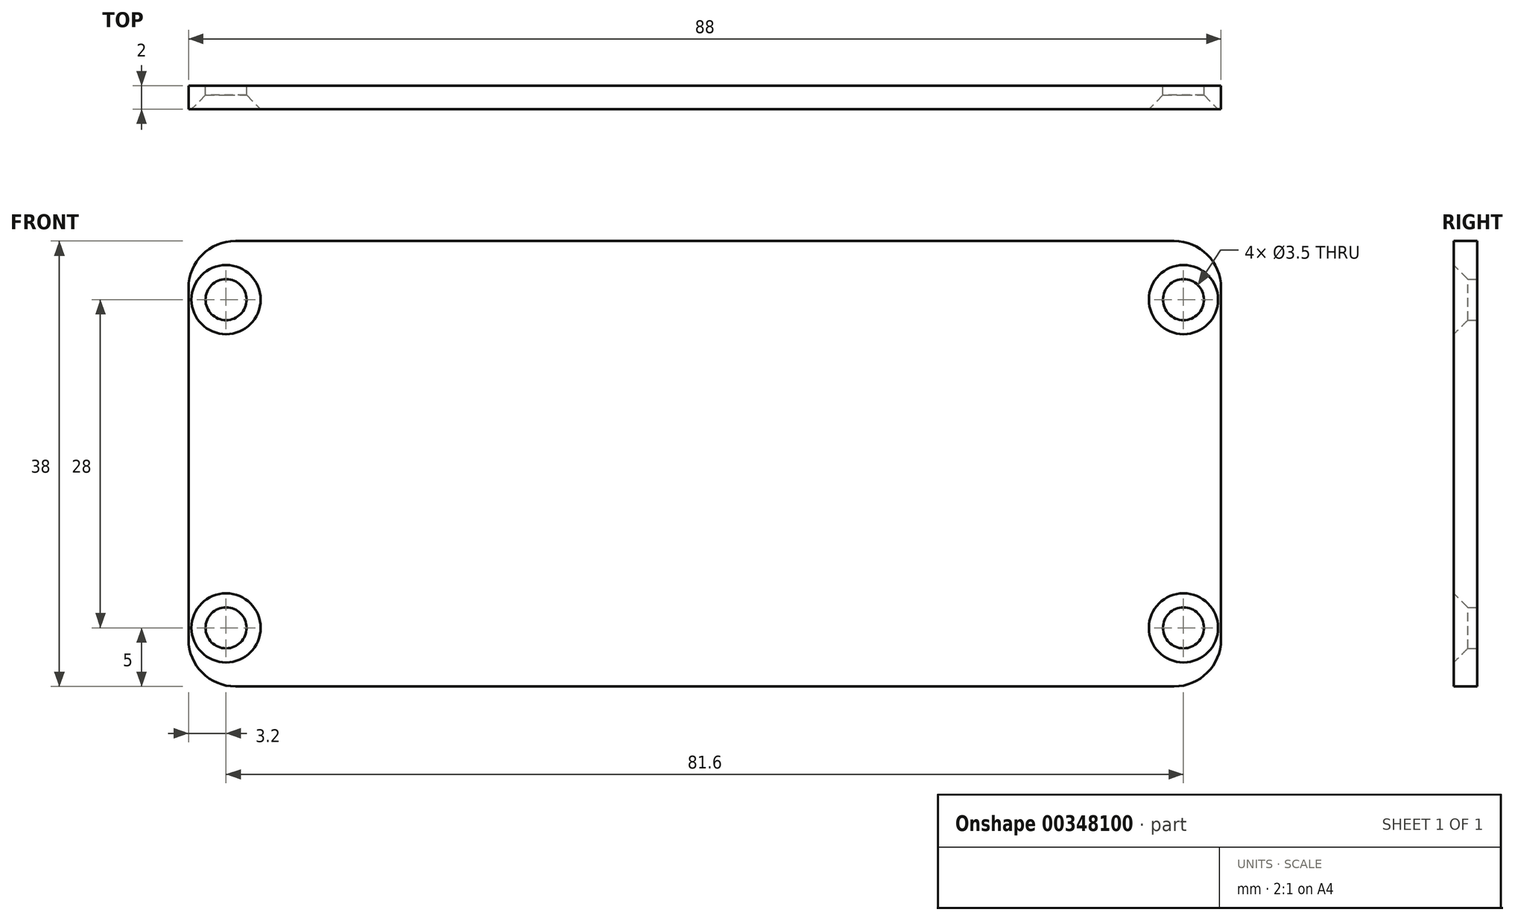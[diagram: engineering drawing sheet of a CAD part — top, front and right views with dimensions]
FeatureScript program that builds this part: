
annotation { "Feature Type Name" : "Feature", "Feature Type Description" : "" }
export const myFeature = defineFeature(function(context is Context, id is Id, definition is map)
    precondition{}
    {
        {
            var Q0;
            Q0=qCreatedBy(makeId("Front.planeOp"),FACE);
            var sketch = newSketch(context, id + "F0", { "sketchPlane" : qUnion([Q0])});
            skLineSegment(sketch, "E0.bottom", {"start": v(-40, 38) * mm, "end": v(40, 38) * mm});
            skLineSegment(sketch, "E0.top", {"start": v(-40, 0) * mm, "end": v(40, 0) * mm});
            skLineSegment(sketch, "E0.left", {"start": v(-44, 34) * mm, "end": v(-44, 4) * mm});
            skLineSegment(sketch, "E0.right", {"start": v(44, 34) * mm, "end": v(44, 4) * mm});
            skPoint(sketch, "E1.visualSharp", {"position": v(-44, 38) * mm});
            skArc(sketch, "E1.filletArc", {"start": v(-40, 38) * mm, "mid": v(-42.83, 36.83) * mm, "end": v(-44, 34) * mm});
            skPoint(sketch, "E2.visualSharp", {"position": v(-44, 0) * mm});
            skArc(sketch, "E2.filletArc", {"start": v(-44, 4) * mm, "mid": v(-42.83, 1.17) * mm, "end": v(-40, 0) * mm});
            skPoint(sketch, "E3.visualSharp", {"position": v(44, 0) * mm});
            skArc(sketch, "E3.filletArc", {"start": v(40, 0) * mm, "mid": v(42.83, 1.17) * mm, "end": v(44, 4) * mm});
            skPoint(sketch, "E4.visualSharp", {"position": v(44, 38) * mm});
            skArc(sketch, "E4.filletArc", {"start": v(44, 34) * mm, "mid": v(42.83, 36.83) * mm, "end": v(40, 38) * mm});
            skCircle(sketch, "E5", {"center": v(-40.8, 5) * mm, "radius": 1.75 * mm});
            skLineSegment(sketch, "E6", {"start": v(-44, 19) * mm, "end": v(44, 19) * mm, "construction": true});
            skCircle(sketch, "E7.MirrorC", {"center": v(-40.8, 33) * mm, "radius": 1.75 * mm});
            skCircle(sketch, "E8.MirrorC", {"center": v(40.8, 5) * mm, "radius": 1.75 * mm});
            skCircle(sketch, "E9.MirrorC", {"center": v(40.8, 33) * mm, "radius": 1.75 * mm});
            skSolve(sketch);
        }
        {
            var Q0;
            Q0 = qSketchRegion(id + "F0", true);
            extrude(context, id + "F1", {"entities" : qUnion([Q0]), "depth" : 2 * mm});
        }
        {
            var Q0;
            Q0=makeQuery(id+"F1.opExtrude","CAP_EDGE",EDGE,{"disambiguationData":[OSD([sQuery(id+"F0.wireOp",EDGE,"E7.MirrorC")])],"isStart":false});
            var Q1;
            Q1=makeQuery(id+"F1.opExtrude","CAP_EDGE",EDGE,{"disambiguationData":[OSD([sQuery(id+"F0.wireOp",EDGE,"E5")])],"isStart":false});
            var Q2;
            Q2=makeQuery(id+"F1.opExtrude","CAP_EDGE",EDGE,{"disambiguationData":[OSD([sQuery(id+"F0.wireOp",EDGE,"E8.MirrorC")])],"isStart":false});
            var Q3;
            Q3=makeQuery(id+"F1.opExtrude","CAP_EDGE",EDGE,{"disambiguationData":[OSD([sQuery(id+"F0.wireOp",EDGE,"E9.MirrorC")])],"isStart":false});
            chamfer(context, id + "F2", {"entities" : qUnion([Q0, Q1, Q2, Q3]), "width" : 1.2 * mm, "tangentPropagation" : true});
        }
    });
